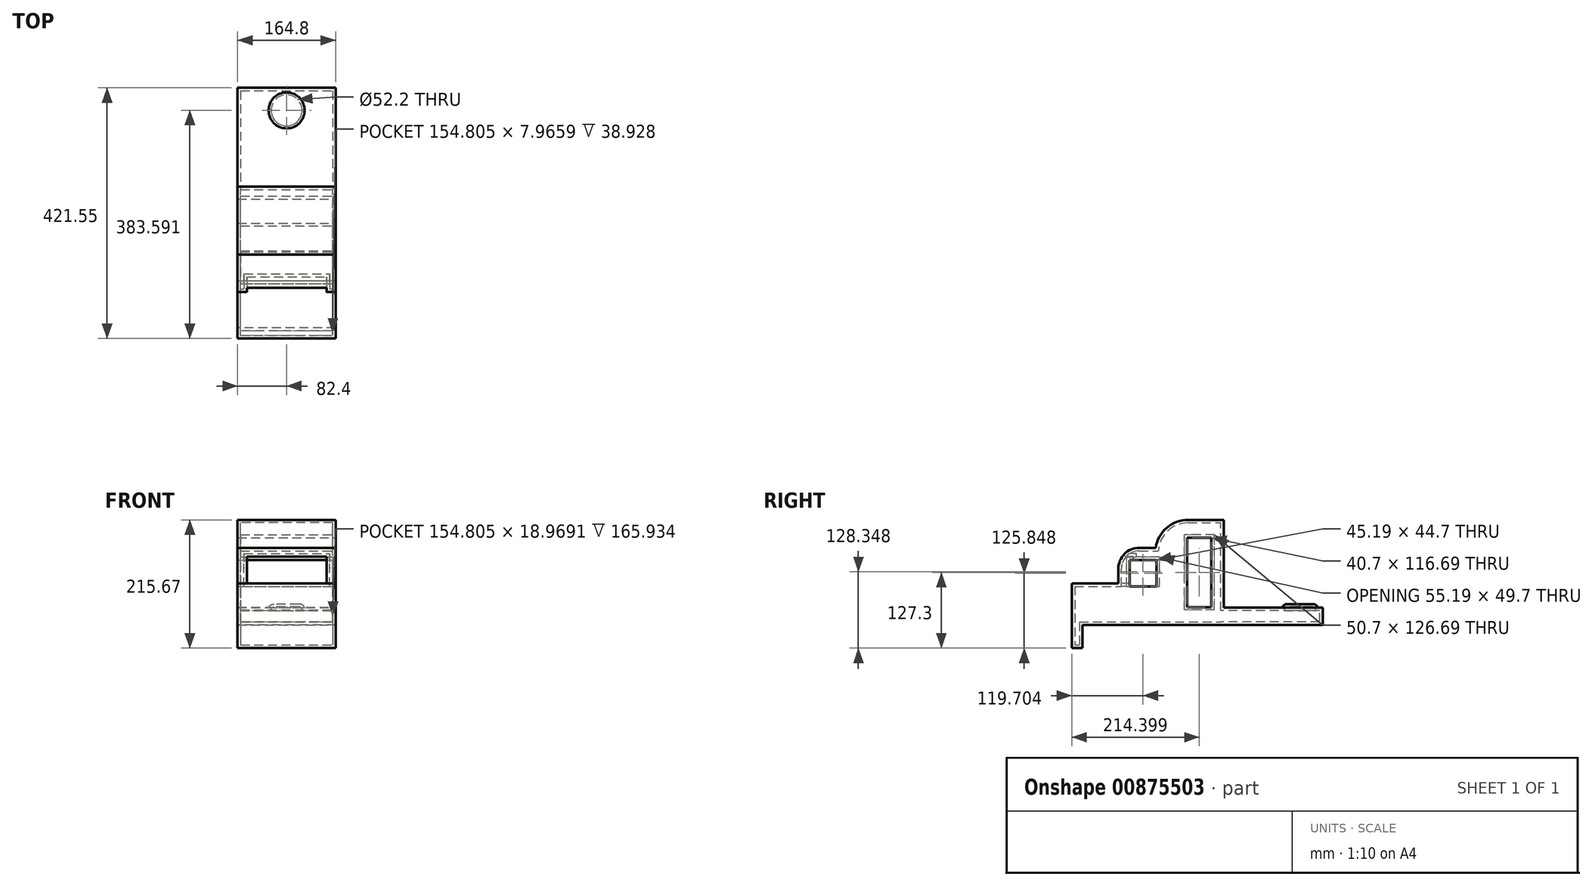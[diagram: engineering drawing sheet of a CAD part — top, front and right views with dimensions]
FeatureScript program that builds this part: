
annotation { "Feature Type Name" : "Feature", "Feature Type Description" : "" }
export const myFeature = defineFeature(function(context is Context, id is Id, definition is map)
    precondition{}
    {
        {
            var Q0;
            Q0=qCreatedBy(makeId("Front.planeOp"),FACE);
            var sketch = newSketch(context, id + "F0", { "sketchPlane" : qUnion([Q0])});
            skLineSegment(sketch, "E0.bottom", {"start": v(77.4, -83.37) * mm, "end": v(-77.4, -83.37) * mm});
            skLineSegment(sketch, "E0.top", {"start": v(77.4, 83.37) * mm, "end": v(-77.4, 83.37) * mm});
            skLineSegment(sketch, "E0.left", {"start": v(77.4, -83.37) * mm, "end": v(77.4, 83.37) * mm});
            skLineSegment(sketch, "E0.right", {"start": v(-77.4, -83.37) * mm, "end": v(-77.4, 83.37) * mm});
            skPoint(sketch, "E0.middle", {"position": v(0, 0) * mm});
            skSolve(sketch);
        }
        {
            var Q0;
            Q0=makeQuery(id+"F0.imprint","IMPRINT",FACE,{"disambiguationData":[TD([[makeQuery(id+"F0.imprint","IMPRINT",EDGE,{"derivedFrom":sQuery(id+"F0.wireOp",EDGE,"E0.bottom")}),-1.0]])]});
            extrude(context, id + "F1", {"entities" : qUnion([Q0]), "depth" : 105.06 * mm, "offsetDistance" : 25.4 * mm});
        }
        {
            var Q0;
            Q0=makeQuery(id+"F1.opExtrude","CAP_FACE",FACE,{"disambiguationData":[OSD([sQuery(id+"F0.wireOp",EDGE,"E0.bottom"),sQuery(id+"F0.wireOp",EDGE,"E0.top"),sQuery(id+"F0.wireOp",EDGE,"E0.left"),sQuery(id+"F0.wireOp",EDGE,"E0.right")])],"isStart":true});
            var sketch = newSketch(context, id + "F2", { "sketchPlane" : qUnion([Q0])});
            skLineSegment(sketch, "E1.bottom", {"start": v(77.4, -64.22) * mm, "end": v(-77.4, -64.22) * mm});
            skLineSegment(sketch, "E1.top", {"start": v(77.4, -83.19) * mm, "end": v(-77.4, -83.19) * mm});
            skLineSegment(sketch, "E1.left", {"start": v(77.4, -64.22) * mm, "end": v(77.4, -83.19) * mm});
            skLineSegment(sketch, "E1.right", {"start": v(-77.4, -64.22) * mm, "end": v(-77.4, -83.19) * mm});
            skPoint(sketch, "E1.middle", {"position": v(0, -73.7) * mm});
            skSolve(sketch);
        }
        {
            var Q0;
            Q0=makeQuery(id+"F2.imprint","IMPRINT",FACE,{"disambiguationData":[TD([[makeQuery(id+"F2.imprint","IMPRINT",EDGE,{"derivedFrom":sQuery(id+"F2.wireOp",EDGE,"E1.bottom")}),1.0]])]});
            extrude(context, id + "F3", {"entities" : qUnion([Q0]), "operationType" : NewBodyOperationType.ADD, "depth" : 165.93 * mm, "offsetDistance" : 25.4 * mm});
        }
        {
            var Q0;
            Q0=makeQuery(id+"F1.opExtrude","CAP_FACE",FACE,{"disambiguationData":[OSD([sQuery(id+"F0.wireOp",EDGE,"E0.bottom"),sQuery(id+"F0.wireOp",EDGE,"E0.top"),sQuery(id+"F0.wireOp",EDGE,"E0.left"),sQuery(id+"F0.wireOp",EDGE,"E0.right")])],"isStart":false});
            var sketch = newSketch(context, id + "F4", { "sketchPlane" : qUnion([Q0])});
            skLineSegment(sketch, "E2.bottom", {"start": v(-77.4, 36.15) * mm, "end": v(77.4, 36.15) * mm});
            skLineSegment(sketch, "E2.top", {"start": v(-77.4, -83.37) * mm, "end": v(77.4, -83.37) * mm});
            skLineSegment(sketch, "E2.left", {"start": v(-77.4, 36.15) * mm, "end": v(-77.4, -83.37) * mm});
            skLineSegment(sketch, "E2.right", {"start": v(77.4, 36.15) * mm, "end": v(77.4, -83.37) * mm});
            skSolve(sketch);
        }
        {
            var Q0;
            Q0=makeQuery(id+"F4.imprint","IMPRINT",FACE,{"disambiguationData":[TD([[makeQuery(id+"F4.imprint","IMPRINT",EDGE,{"derivedFrom":sQuery(id+"F4.wireOp",EDGE,"E2.bottom")}),-1.0]])]});
            extrude(context, id + "F5", {"entities" : qUnion([Q0]), "operationType" : NewBodyOperationType.ADD, "depth" : 62.22 * mm, "offsetDistance" : 25.4 * mm});
        }
        {
            var Q0;
            Q0=makeQuery(id+"F1.opExtrude","CAP_EDGE",EDGE,{"disambiguationData":[OSD([sQuery(id+"F0.wireOp",EDGE,"E0.top")])],"isStart":false});
            fillet(context, id + "F6", {"entities" : qUnion([Q0]), "radius" : 50 * mm, "tangentPropagation" : true, "allowEdgeOverflow" : false});
        }
        {
            var Q0;
            Q0=makeQuery(id+"F5.opExtrude","CAP_FACE",FACE,{"disambiguationData":[OSD([sQuery(id+"F4.wireOp",EDGE,"E2.bottom"),sQuery(id+"F4.wireOp",EDGE,"E2.top"),sQuery(id+"F4.wireOp",EDGE,"E2.left"),sQuery(id+"F4.wireOp",EDGE,"E2.right")])],"isStart":false});
            var sketch = newSketch(context, id + "F7", { "sketchPlane" : qUnion([Q0])});
            skLineSegment(sketch, "E3.bottom", {"start": v(-77.4, -23.6) * mm, "end": v(77.4, -23.6) * mm});
            skLineSegment(sketch, "E3.top", {"start": v(-77.4, -83.37) * mm, "end": v(77.4, -83.37) * mm});
            skLineSegment(sketch, "E3.left", {"start": v(-77.4, -23.6) * mm, "end": v(-77.4, -83.37) * mm});
            skLineSegment(sketch, "E3.right", {"start": v(77.4, -23.6) * mm, "end": v(77.4, -83.37) * mm});
            skSolve(sketch);
        }
        {
            var Q0;
            Q0=makeQuery(id+"F7.imprint","IMPRINT",FACE,{"disambiguationData":[TD([[makeQuery(id+"F7.imprint","IMPRINT",EDGE,{"derivedFrom":sQuery(id+"F7.wireOp",EDGE,"E3.bottom")}),-1.0]])]});
            var Q1;
            Q1 = qSketchRegion(id + "F7", true);
            extrude(context, id + "F8", {"entities" : qUnion([Q0, Q1]), "operationType" : NewBodyOperationType.ADD, "depth" : 70.38 * mm, "offsetDistance" : 25.4 * mm});
        }
        {
            var Q0;
            Q0=makeQuery(id+"F8.opExtrude","CAP_FACE",FACE,{"disambiguationData":[OSD([sQuery(id+"F7.wireOp",EDGE,"E3.bottom"),sQuery(id+"F7.wireOp",EDGE,"E3.top"),sQuery(id+"F7.wireOp",EDGE,"E3.left"),sQuery(id+"F7.wireOp",EDGE,"E3.right")])],"isStart":false});
            var sketch = newSketch(context, id + "F9", { "sketchPlane" : qUnion([Q0])});
            skLineSegment(sketch, "E4.bottom", {"start": v(-77.4, -53.49) * mm, "end": v(77.4, -53.49) * mm});
            skLineSegment(sketch, "E4.top", {"start": v(-77.4, -122.3) * mm, "end": v(77.4, -122.3) * mm});
            skLineSegment(sketch, "E4.left", {"start": v(-77.4, -53.49) * mm, "end": v(-77.4, -122.3) * mm});
            skLineSegment(sketch, "E4.right", {"start": v(77.4, -53.49) * mm, "end": v(77.4, -122.3) * mm});
            skSolve(sketch);
        }
        {
            var Q0;
            {var subQ0=sQuery(id+"F9.wireOp",EDGE,"E4.top");Q0=makeQuery(id+"F9.imprint","IMPRINT",FACE,{"disambiguationData":[TD([[makeQuery(id+"F9.imprint","IMPRINT",EDGE,{"derivedFrom":subQ0}),1.0]])]});}
            var Q1;
            {var subQ0=sQuery(id+"F9.wireOp",EDGE,"E4.bottom");Q1=makeQuery(id+"F9.imprint","IMPRINT",FACE,{"disambiguationData":[TD([[makeQuery(id+"F9.imprint","IMPRINT",EDGE,{"derivedFrom":subQ0}),-1.0]])]});}
            var Q2;
            {var subQ0=sQuery(id+"F9.wireOp",EDGE,"E4.bottom");Q2=makeQuery(id+"F9.imprint","IMPRINT",FACE,{"disambiguationData":[TD([[makeQuery(id+"F9.imprint","IMPRINT",EDGE,{"derivedFrom":subQ0}),1.0]])]});}
            extrude(context, id + "F10", {"entities" : qUnion([Q0, Q1, Q2]), "operationType" : NewBodyOperationType.ADD, "depth" : 7.97 * mm, "offsetDistance" : 25.4 * mm});
        }
        {
            var Q0;
            Q0=makeQuery(id+"F5.opExtrude","CAP_EDGE",EDGE,{"disambiguationData":[OSD([sQuery(id+"F4.wireOp",EDGE,"E2.bottom")])],"isStart":false});
            fillet(context, id + "F11", {"entities" : qUnion([Q0]), "radius" : 30 * mm, "tangentPropagation" : true, "allowEdgeOverflow" : false});
        }
        {
            var Q0;
            Q0=makeQuery(id+"F3.opExtrude","SWEPT_FACE",FACE,{"disambiguationData":[OSD([sQuery(id+"F2.wireOp",EDGE,"E1.bottom")])]});
            var sketch = newSketch(context, id + "F12", { "sketchPlane" : qUnion([Q0])});
            skCircle(sketch, "E5", {"center": v(0, 132.97) * mm, "radius": 26.1 * mm});
            skSolve(sketch);
        }
        {
            var Q0;
            Q0=makeQuery(id+"F12.imprint","IMPRINT",FACE,{"disambiguationData":[TD([[makeQuery(id+"F12.imprint","IMPRINT",EDGE,{"derivedFrom":sQuery(id+"F12.wireOp",EDGE,"E5")}),1.0]])]});
            extrude(context, id + "F13", {"entities" : qUnion([Q0]), "operationType" : NewBodyOperationType.ADD, "depth" : 5.98 * mm, "offsetDistance" : 25.4 * mm});
        }
        {
            var Q0;
            Q0=makeQuery(id+"F13.opExtrude","CAP_EDGE",EDGE,{"disambiguationData":[OSD([sQuery(id+"F12.wireOp",EDGE,"E5")])],"isStart":false});
            fillet(context, id + "F14", {"entities" : qUnion([Q0]), "radius" : 5.08 * mm, "tangentPropagation" : true, "allowEdgeOverflow" : false});
        }
        {
            var Q0;
            {var subQ0=sQuery(id+"F7.wireOp",EDGE,"E3.right");Q0=makeQuery(id+"F10.boolean.opBoolean","MERGE",FACE,{"derivedFrom":[makeQuery(id+"F8.boolean.opBoolean","MERGE",FACE,{"derivedFrom":[makeQuery(id+"F5.boolean.opBoolean","MERGE",FACE,{"derivedFrom":[makeQuery(id+"F3.boolean.opBoolean","MERGE",FACE,{"derivedFrom":[makeQuery(id+"F1.opExtrude","SWEPT_FACE",FACE,{"disambiguationData":[OSD([sQuery(id+"F0.wireOp",EDGE,"E0.left")])]}),makeQuery(id+"F3.opExtrude","SWEPT_FACE",FACE,{"disambiguationData":[OSD([sQuery(id+"F2.wireOp",EDGE,"E1.right")])]})]}),makeQuery(id+"F5.opExtrude","SWEPT_FACE",FACE,{"disambiguationData":[OSD([sQuery(id+"F4.wireOp",EDGE,"E2.right")])]})]}),makeQuery(id+"F8.opExtrude","SWEPT_FACE",FACE,{"disambiguationData":[OSD([subQ0])]})]}),makeQuery(id+"F10.opExtrude","SWEPT_FACE",FACE,{"disambiguationData":[OSD([subQ0,sQuery(id+"F9.wireOp",EDGE,"E4.right")])]})]});}
            var sketch = newSketch(context, id + "F15", { "sketchPlane" : qUnion([Q0])});
            skLineSegment(sketch, "E6.bottom", {"start": v(-10.87, -63.35) * mm, "end": v(-61.57, -63.35) * mm});
            skLineSegment(sketch, "E6.top", {"start": v(-10.87, 63.35) * mm, "end": v(-61.57, 63.35) * mm});
            skLineSegment(sketch, "E6.left", {"start": v(-10.87, -63.35) * mm, "end": v(-10.87, 63.35) * mm});
            skLineSegment(sketch, "E6.right", {"start": v(-61.57, -63.35) * mm, "end": v(-61.57, 63.35) * mm});
            skPoint(sketch, "E6.middle", {"position": v(-36.22, 0) * mm});
            skSolve(sketch);
        }
        {
            var Q0;
            Q0=makeQuery(id+"F15.imprint","IMPRINT",FACE,{"disambiguationData":[TD([[makeQuery(id+"F15.imprint","IMPRINT",EDGE,{"derivedFrom":sQuery(id+"F15.wireOp",EDGE,"E6.bottom")}),-1.0]])]});
            extrude(context, id + "F16", {"entities" : qUnion([Q0]), "operationType" : NewBodyOperationType.REMOVE, "oppositeDirection" : true, "depth" : 277.14 * mm, "offsetDistance" : 25.4 * mm});
        }
        {
            var Q0;
            {var subQ0=sQuery(id+"F7.wireOp",EDGE,"E3.right");Q0=makeQuery(id+"F10.boolean.opBoolean","MERGE",FACE,{"derivedFrom":[makeQuery(id+"F8.boolean.opBoolean","MERGE",FACE,{"derivedFrom":[makeQuery(id+"F5.boolean.opBoolean","MERGE",FACE,{"derivedFrom":[makeQuery(id+"F3.boolean.opBoolean","MERGE",FACE,{"derivedFrom":[makeQuery(id+"F1.opExtrude","SWEPT_FACE",FACE,{"disambiguationData":[OSD([sQuery(id+"F0.wireOp",EDGE,"E0.left")])]}),makeQuery(id+"F3.opExtrude","SWEPT_FACE",FACE,{"disambiguationData":[OSD([sQuery(id+"F2.wireOp",EDGE,"E1.right")])]})]}),makeQuery(id+"F5.opExtrude","SWEPT_FACE",FACE,{"disambiguationData":[OSD([sQuery(id+"F4.wireOp",EDGE,"E2.right")])]})]}),makeQuery(id+"F8.opExtrude","SWEPT_FACE",FACE,{"disambiguationData":[OSD([subQ0])]})]}),makeQuery(id+"F10.opExtrude","SWEPT_FACE",FACE,{"disambiguationData":[OSD([subQ0,sQuery(id+"F9.wireOp",EDGE,"E4.right")])]})]});}
            var sketch = newSketch(context, id + "F17", { "sketchPlane" : qUnion([Q0])});
            skLineSegment(sketch, "E7", {"start": v(-158.51, -23.8) * mm, "end": v(-103.32, -23.8) * mm});
            skLineSegment(sketch, "E8", {"start": v(-103.32, -23.8) * mm, "end": v(-103.32, 25.9) * mm});
            skLineSegment(sketch, "E9", {"start": v(-103.32, 25.9) * mm, "end": v(-158.51, 25.9) * mm});
            skLineSegment(sketch, "E10", {"start": v(-158.51, 25.9) * mm, "end": v(-158.51, -23.8) * mm});
            skSolve(sketch);
        }
        {
            var Q0;
            Q0=makeQuery(id+"F17.imprint","IMPRINT",FACE,{"disambiguationData":[TD([[makeQuery(id+"F17.imprint","IMPRINT",EDGE,{"derivedFrom":sQuery(id+"F17.wireOp",EDGE,"E7")}),1.0]])]});
            extrude(context, id + "F18", {"entities" : qUnion([Q0]), "operationType" : NewBodyOperationType.REMOVE, "oppositeDirection" : true, "depth" : 220.06 * mm, "offsetDistance" : 25.4 * mm});
        }
        {
            var Q0;
            Q0=makeQuery(id+"F5.opExtrude","CAP_FACE",FACE,{"disambiguationData":[OSD([sQuery(id+"F4.wireOp",EDGE,"E2.bottom"),sQuery(id+"F4.wireOp",EDGE,"E2.top"),sQuery(id+"F4.wireOp",EDGE,"E2.left"),sQuery(id+"F4.wireOp",EDGE,"E2.right")])],"isStart":false});
            var sketch = newSketch(context, id + "F19", { "sketchPlane" : qUnion([Q0])});
            skLineSegment(sketch, "E11.bottom", {"start": v(-71.79, -23.6) * mm, "end": v(72.17, -23.6) * mm});
            skLineSegment(sketch, "E11.top", {"start": v(-71.79, 31.66) * mm, "end": v(72.17, 31.66) * mm});
            skLineSegment(sketch, "E11.left", {"start": v(-71.79, -23.6) * mm, "end": v(-71.79, 31.66) * mm});
            skLineSegment(sketch, "E11.right", {"start": v(72.17, -23.6) * mm, "end": v(72.17, 31.66) * mm});
            skSolve(sketch);
        }
        {
            var Q0;
            {var subQ0=sQuery(id+"F19.wireOp",EDGE,"E11.bottom");Q0=makeQuery(id+"F19.imprint","IMPRINT",FACE,{"disambiguationData":[TD([[makeQuery(id+"F19.imprint","IMPRINT",EDGE,{"derivedFrom":subQ0}),1.0]])]});}
            var Q1;
            {var subQ0=sQuery(id+"F19.wireOp",EDGE,"E11.top");Q1=makeQuery(id+"F19.imprint","IMPRINT",FACE,{"disambiguationData":[TD([[makeQuery(id+"F19.imprint","IMPRINT",EDGE,{"derivedFrom":subQ0}),-1.0]])]});}
            extrude(context, id + "F20", {"entities" : qUnion([Q0, Q1]), "operationType" : NewBodyOperationType.REMOVE, "oppositeDirection" : true, "depth" : 25.4 * mm, "offsetDistance" : 25.4 * mm});
        }
        {
            var Q0;
            Q0=makeQuery(id+"F18.boolean.opBoolean","COPY",FACE,{"derivedFrom":makeQuery(id+"F18.opExtrude","SWEPT_FACE",FACE,{"disambiguationData":[OSD([sQuery(id+"F17.wireOp",EDGE,"E7")])]})});
            shell(context, id + "F21", {"entities" : qUnion([Q0]), "thickness" : 5 * mm, "oppositeDirection" : true});
        }
        {
            var Q0;
            {var subQ0=sQuery(id+"F7.wireOp",EDGE,"E3.right");Q0=makeQuery(id+"F10.boolean.opBoolean","MERGE",FACE,{"derivedFrom":[makeQuery(id+"F8.boolean.opBoolean","MERGE",FACE,{"derivedFrom":[makeQuery(id+"F5.boolean.opBoolean","MERGE",FACE,{"derivedFrom":[makeQuery(id+"F3.boolean.opBoolean","MERGE",FACE,{"derivedFrom":[makeQuery(id+"F1.opExtrude","SWEPT_FACE",FACE,{"disambiguationData":[OSD([sQuery(id+"F0.wireOp",EDGE,"E0.left")])]}),makeQuery(id+"F3.opExtrude","SWEPT_FACE",FACE,{"disambiguationData":[OSD([sQuery(id+"F2.wireOp",EDGE,"E1.right")])]})]}),makeQuery(id+"F5.opExtrude","SWEPT_FACE",FACE,{"disambiguationData":[OSD([sQuery(id+"F4.wireOp",EDGE,"E2.right")])]})]}),makeQuery(id+"F8.opExtrude","SWEPT_FACE",FACE,{"disambiguationData":[OSD([subQ0])]})]}),makeQuery(id+"F10.opExtrude","SWEPT_FACE",FACE,{"disambiguationData":[OSD([subQ0,sQuery(id+"F9.wireOp",EDGE,"E4.right")])]})]});}
            cPlane(context, id + "F22", {"entities" : qUnion([Q0]), "cplaneType" : CPlaneType.OFFSET, "offset" : 25.4 * mm, "width" : 152.4 * mm, "height" : 152.4 * mm});
        }
    });
